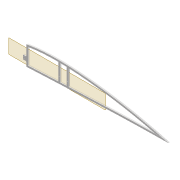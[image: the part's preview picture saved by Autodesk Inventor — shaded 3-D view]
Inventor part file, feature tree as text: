
AUTODESK INVENTOR PART (.ipt)
format: ipt  version: 2022 (Build 260153000, 153)  size: 422,400 bytes
history: native  units: mm
features: extrude x8, sketch x7, projected_geometry x6, fillet x2, shell x1, plane x1
ambient origin geometry x8: Origin, YZ Plane, XZ Plane, XY Plane, X Axis, Y Axis, Z Axis, Center Point
bodies: Solid1 (feature_tree)
feature tree (25):
  extrude  "Extrusion1"  Depth=5.0mm
  shell  "Shell1"  Thickness=2.0mm
  extrude  "Extrusion8"  Depth=5.9mm
  extrude  "Extrusion3"  Depth=10.0mm TaperAngle=0.0deg
  extrude  "Extrusion4"  Depth=2.0mm
  fillet  "Fillet1"  Radius=5.0mm
  sketch  "Sketch10"  dims[d22=4.0mm d23=0.0mm d31=2.0mm d32=5.0mm]
  extrude  "Extrusion5"  Depth=2.5mm
  plane  "Work Plane2"
  extrude  "Extrusion9"  Depth=1.6mm
  fillet  "Fillet2"  Radius=2.5mm
  extrude  "Extrusion10"  Depth=0.5mm
  extrude  "Extrusion11"  Depth=0.5mm TaperAngle=0.0deg
  sketch  "Sketch3"  dims[d0=4.0mm d1=0.0mm d2=5.0mm d7=2.0mm]
  sketch  "Sketch8"  dims[d8=2.0mm d9=5.9mm]
  sketch  "Sketch9"  dims[d13=10.0mm d14=0.0mm d16=10.0mm d17=0.0mm]
  projected_geometry  "Projected Loop4"
  projected_geometry  "Projected Loop10"
  sketch  "Sketch24"  dims[d34=1.6mm d35=2.5mm]
  projected_geometry  "Projected Loop11"
  projected_geometry  "Projected Loop12"
  projected_geometry  "Projected Loop13"
  sketch  "Sketch26"  dims[d37=5.0mm d38=1.6mm d40=2.5mm]
  projected_geometry  "Projected Loop14"
  sketch  "Sketch27"  dims[d62=80.0mm d63=6.0mm d64=4.0mm d65=0.0mm d66=3.0mm d67=12.0mm d68=5.0mm d69=10.0mm d70=12.0mm d71=3.05mm d72=10.0mm d73=0.0mm d74=2.0mm d75=100.0mm d76=20.0mm d77=0.5mm d78=10.0mm d79=0.0mm d80=10.0mm d81=0.0mm]
